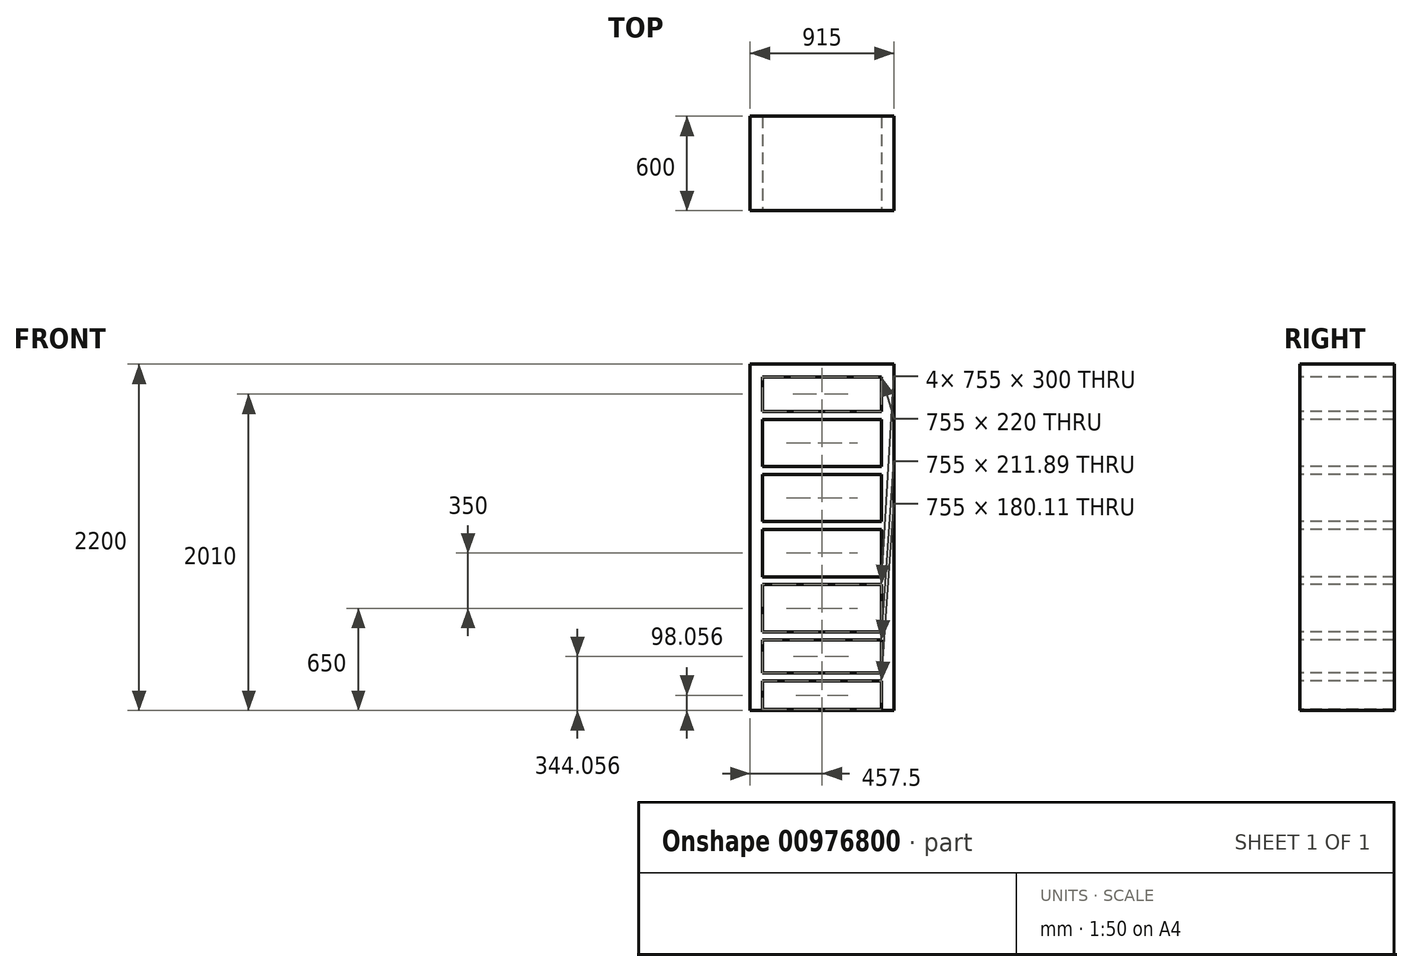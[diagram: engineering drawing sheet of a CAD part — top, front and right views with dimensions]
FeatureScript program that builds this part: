
annotation { "Feature Type Name" : "Feature", "Feature Type Description" : "" }
export const myFeature = defineFeature(function(context is Context, id is Id, definition is map)
    precondition{}
    {
        {
            var Q0;
            Q0=qCreatedBy(makeId("Front.planeOp"),FACE);
            var sketch = newSketch(context, id + "F0", { "sketchPlane" : qUnion([Q0])});
            skLineSegment(sketch, "E0", {"start": v(0, 1079.8) * mm, "end": v(0, -799.99) * mm, "construction": true});
            skLineSegment(sketch, "E1", {"start": v(-1169.75, 0) * mm, "end": v(1371, 0) * mm, "construction": true});
            skLineSegment(sketch, "E2.bottom", {"start": v(-457.5, 1100) * mm, "end": v(457.5, 1100) * mm});
            skLineSegment(sketch, "E2.top", {"start": v(-457.5, -1100) * mm, "end": v(457.5, -1100) * mm});
            skLineSegment(sketch, "E2.left", {"start": v(-457.5, 1100) * mm, "end": v(-457.5, -1100) * mm});
            skLineSegment(sketch, "E2.right", {"start": v(457.5, 1100) * mm, "end": v(457.5, -1100) * mm});
            skSolve(sketch);
        }
        {
            var Q0;
            Q0 = qSketchRegion(id + "F0", true);
            extrude(context, id + "F1", {"entities" : qUnion([Q0]), "depth" : 600 * mm, "offsetDistance" : 25.4 * mm});
        }
        {
            var Q0;
            Q0=makeQuery(id+"F1.opExtrude","CAP_FACE",FACE,{"disambiguationData":[OSD([sQuery(id+"F0.wireOp",EDGE,"E2.bottom"),sQuery(id+"F0.wireOp",EDGE,"E2.top"),sQuery(id+"F0.wireOp",EDGE,"E2.left"),sQuery(id+"F0.wireOp",EDGE,"E2.right")])],"isStart":false});
            var sketch = newSketch(context, id + "F2", { "sketchPlane" : qUnion([Q0])});
            skLineSegment(sketch, "E3.bottom", {"start": v(-377.5, 800) * mm, "end": v(377.5, 800) * mm});
            skLineSegment(sketch, "E3.top", {"start": v(-377.5, 750) * mm, "end": v(377.5, 750) * mm});
            skLineSegment(sketch, "E3.left", {"start": v(-457.5, 800) * mm, "end": v(-457.5, 750) * mm});
            skLineSegment(sketch, "E3.right", {"start": v(457.5, 800) * mm, "end": v(457.5, 750) * mm});
            skLineSegment(sketch, "E4.bottom", {"start": v(-377.5, 450) * mm, "end": v(377.5, 450) * mm});
            skLineSegment(sketch, "E4.top", {"start": v(-377.5, 400) * mm, "end": v(377.5, 400) * mm});
            skLineSegment(sketch, "E4.left", {"start": v(-457.5, 450) * mm, "end": v(-457.5, 400) * mm});
            skLineSegment(sketch, "E4.right", {"start": v(457.5, 450) * mm, "end": v(457.5, 400) * mm});
            skLineSegment(sketch, "E5.bottom", {"start": v(-377.5, 100) * mm, "end": v(377.5, 100) * mm});
            skLineSegment(sketch, "E5.top", {"start": v(-377.5, 50) * mm, "end": v(377.5, 50) * mm});
            skLineSegment(sketch, "E5.left", {"start": v(-457.5, 100) * mm, "end": v(-457.5, 50) * mm});
            skLineSegment(sketch, "E5.right", {"start": v(457.5, 100) * mm, "end": v(457.5, 50) * mm});
            skLineSegment(sketch, "E6.bottom", {"start": v(-377.5, -250) * mm, "end": v(377.5, -250) * mm});
            skLineSegment(sketch, "E6.top", {"start": v(-377.5, -300) * mm, "end": v(377.5, -300) * mm});
            skLineSegment(sketch, "E6.left", {"start": v(-457.5, -250) * mm, "end": v(-457.5, -300) * mm});
            skLineSegment(sketch, "E6.right", {"start": v(457.5, -250) * mm, "end": v(457.5, -300) * mm});
            skLineSegment(sketch, "E7.bottom", {"start": v(-377.5, -600) * mm, "end": v(377.5, -600) * mm});
            skLineSegment(sketch, "E7.top", {"start": v(-377.5, -650) * mm, "end": v(377.5, -650) * mm});
            skLineSegment(sketch, "E7.left", {"start": v(-457.5, -600) * mm, "end": v(-457.5, -650) * mm});
            skLineSegment(sketch, "E7.right", {"start": v(457.5, -600) * mm, "end": v(457.5, -650) * mm});
            skLineSegment(sketch, "E8.bottom", {"start": v(-377.5, -861.89) * mm, "end": v(377.5, -861.89) * mm});
            skLineSegment(sketch, "E8.top", {"start": v(-377.5, -911.89) * mm, "end": v(377.5, -911.89) * mm});
            skLineSegment(sketch, "E8.left", {"start": v(-457.5, -861.89) * mm, "end": v(-457.5, -911.89) * mm});
            skLineSegment(sketch, "E8.right", {"start": v(457.5, -861.89) * mm, "end": v(457.5, -911.89) * mm});
            skLineSegment(sketch, "E9", {"start": v(-377.5, 1100) * mm, "end": v(-377.5, -1100) * mm});
            skLineSegment(sketch, "E10", {"start": v(377.5, 1100) * mm, "end": v(377.5, -1100) * mm});
            skLineSegment(sketch, "E11.bottom", {"start": v(-377.5, 1100) * mm, "end": v(377.5, 1100) * mm});
            skLineSegment(sketch, "E11.top", {"start": v(-377.5, 1020) * mm, "end": v(377.5, 1020) * mm});
            skLineSegment(sketch, "E11.left", {"start": v(-377.5, 1100) * mm, "end": v(-377.5, 1020) * mm});
            skLineSegment(sketch, "E11.right", {"start": v(377.5, 1100) * mm, "end": v(377.5, 1020) * mm});
            skLineSegment(sketch, "E12.bottom", {"start": v(-377.5, -1100) * mm, "end": v(377.5, -1100) * mm});
            skLineSegment(sketch, "E12.top", {"start": v(-377.5, -1092) * mm, "end": v(377.5, -1092) * mm});
            skLineSegment(sketch, "E12.left", {"start": v(-377.5, -1100) * mm, "end": v(-377.5, -1092) * mm});
            skLineSegment(sketch, "E12.right", {"start": v(377.5, -1100) * mm, "end": v(377.5, -1092) * mm});
            skSolve(sketch);
        }
        {
            var Q0;
            {var subQ0=sQuery(id+"F2.wireOp",EDGE,"E3.bottom");Q0=makeQuery(id+"F2.imprint","IMPRINT",FACE,{"disambiguationData":[TD([[makeQuery(id+"F2.imprint","IMPRINT",EDGE,{"derivedFrom":subQ0}),1.0]])]});}
            var Q1;
            {var subQ0=sQuery(id+"F2.wireOp",EDGE,"E3.top");Q1=makeQuery(id+"F2.imprint","IMPRINT",FACE,{"disambiguationData":[TD([[makeQuery(id+"F2.imprint","IMPRINT",EDGE,{"derivedFrom":subQ0}),-1.0]])]});}
            var Q2;
            {var subQ0=sQuery(id+"F2.wireOp",EDGE,"E4.top");Q2=makeQuery(id+"F2.imprint","IMPRINT",FACE,{"disambiguationData":[TD([[makeQuery(id+"F2.imprint","IMPRINT",EDGE,{"derivedFrom":subQ0}),-1.0]])]});}
            var Q3;
            {var subQ0=sQuery(id+"F2.wireOp",EDGE,"E5.top");Q3=makeQuery(id+"F2.imprint","IMPRINT",FACE,{"disambiguationData":[TD([[makeQuery(id+"F2.imprint","IMPRINT",EDGE,{"derivedFrom":subQ0}),-1.0]])]});}
            var Q4;
            {var subQ0=sQuery(id+"F2.wireOp",EDGE,"E6.top");Q4=makeQuery(id+"F2.imprint","IMPRINT",FACE,{"disambiguationData":[TD([[makeQuery(id+"F2.imprint","IMPRINT",EDGE,{"derivedFrom":subQ0}),-1.0]])]});}
            var Q5;
            {var subQ0=sQuery(id+"F2.wireOp",EDGE,"E7.top");Q5=makeQuery(id+"F2.imprint","IMPRINT",FACE,{"disambiguationData":[TD([[makeQuery(id+"F2.imprint","IMPRINT",EDGE,{"derivedFrom":subQ0}),-1.0]])]});}
            var Q6;
            {var subQ0=sQuery(id+"F2.wireOp",EDGE,"E8.top");Q6=makeQuery(id+"F2.imprint","IMPRINT",FACE,{"disambiguationData":[TD([[makeQuery(id+"F2.imprint","IMPRINT",EDGE,{"derivedFrom":subQ0}),-1.0]])]});}
            extrude(context, id + "F3", {"entities" : qUnion([Q0, Q1, Q2, Q3, Q4, Q5, Q6]), "operationType" : NewBodyOperationType.REMOVE, "endBound" : BoundingType.UP_TO_NEXT, "oppositeDirection" : true, "depth" : 580 * mm, "offsetDistance" : 25.4 * mm});
        }
    });
